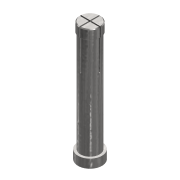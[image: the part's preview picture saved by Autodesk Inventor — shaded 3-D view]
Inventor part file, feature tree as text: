
AUTODESK INVENTOR PART (.ipt)
format: ipt  version: 2020 (Build 240168000, 168)  size: 140,800 bytes
history: native  units: mm
features: extrude x4, sketch x4, chamfer x1, pattern_circular x1
ambient origin geometry x8: Origin, YZ Plane, XZ Plane, XY Plane, X Axis, Y Axis, Z Axis, Center Point
bodies: Solid1 (feature_tree)
feature tree (10):
  extrude  "Extrusion1"  Depth=0.605mm TaperAngle=0.0deg
  extrude  "Extrusion2"  Depth=6.96mm TaperAngle=0.0deg
  extrude  "Extrusion3"  Depth=0.6875mm TaperAngle=0.0deg
  chamfer  "Chamfer1"  Distance=0.055mm Angle=45.0deg
  extrude  "Extrusion4"  Depth=0.041249mm
  pattern_circular  "Circular Pattern1"  [2 undecoded]
  sketch  "Sketch1"  dims[d0=1.65mm d1=0.605mm d2=0.0mm]
  sketch  "Sketch2"  dims[d3=1.32mm d4=6.96mm d5=0.0mm]
  sketch  "Sketch3"  dims[d6=1.43mm d7=0.6875mm d8=0.0mm d9=0.055mm d10=2.0mm d11=45.0deg]
  sketch  "Sketch4"  dims[d12=0.041249mm d13=2.75mm d14=2.1875mm d15=0.0mm d16=40.0mm d17=360.0deg]
note: 2 required parameter values undecoded (feature->parameter linkage not recoverable at this tier; creation-order binding heuristic only, values carry confidence <= 0.55)
